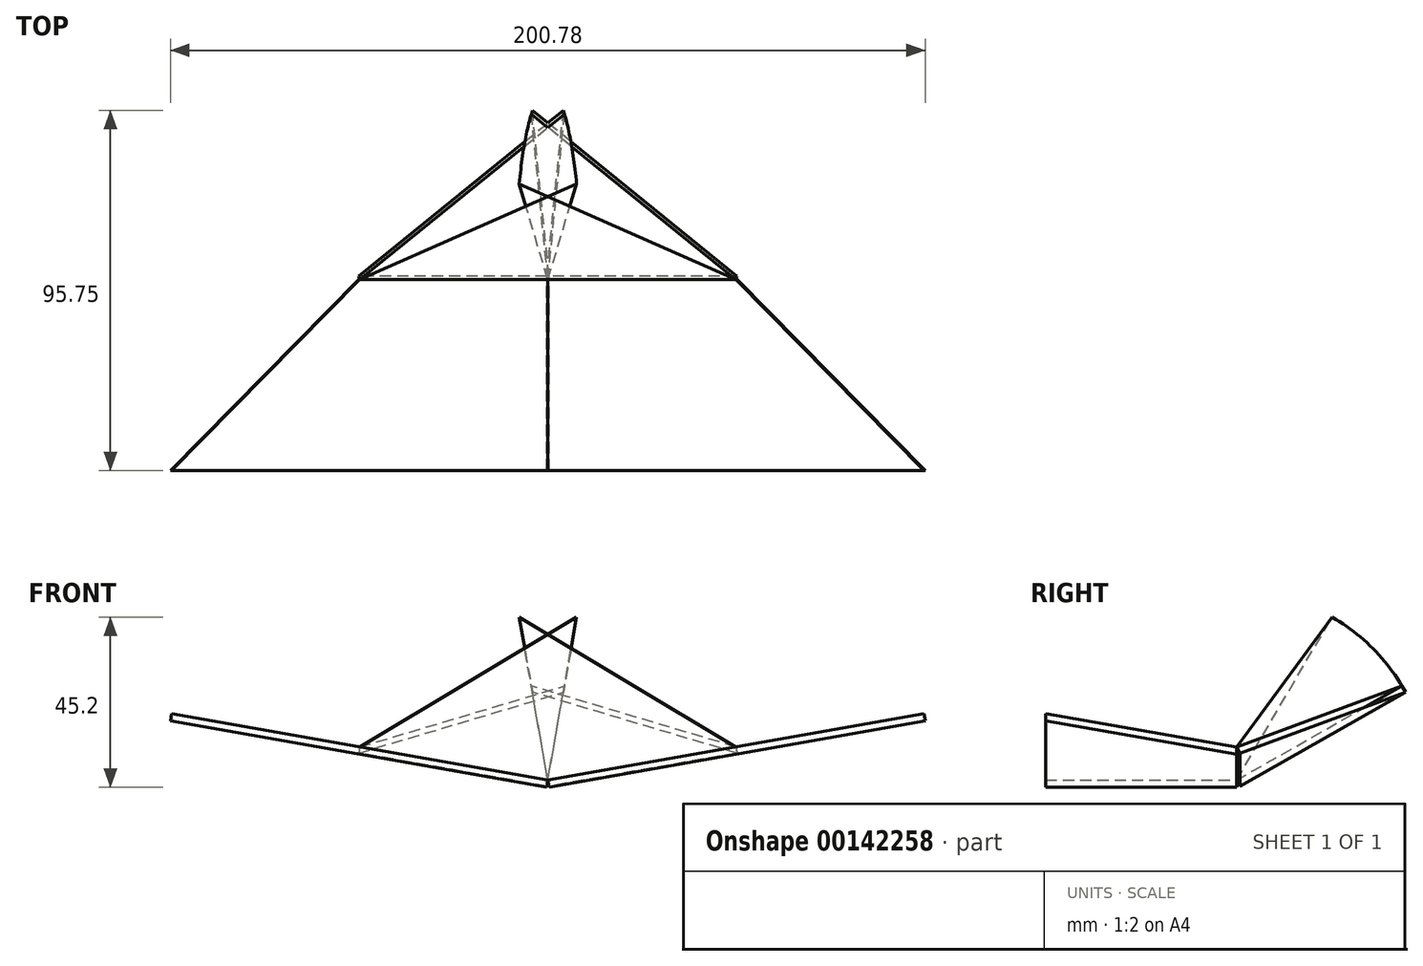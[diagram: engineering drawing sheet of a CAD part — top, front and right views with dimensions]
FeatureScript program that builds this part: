
annotation { "Feature Type Name" : "Feature", "Feature Type Description" : "" }
export const myFeature = defineFeature(function(context is Context, id is Id, definition is map)
    precondition{}
    {
        {
            var Q0;
            Q0=qCreatedBy(makeId("Top.planeOp"),FACE);
            var sketch = newSketch(context, id + "F0", { "sketchPlane" : qUnion([Q0])});
            skLineSegment(sketch, "E0", {"start": v(-101.6, 0) * mm, "end": v(0, 0) * mm});
            skLineSegment(sketch, "E1", {"start": v(-101.6, 0) * mm, "end": v(-50.8, 50.8) * mm});
            skLineSegment(sketch, "E2", {"start": v(101.6, 0) * mm, "end": v(50.8, 50.8) * mm});
            skPoint(sketch, "E3", {"position": v(0, 0) * mm});
            skLineSegment(sketch, "E4", {"start": v(0, 0) * mm, "end": v(0, 50.8) * mm});
            skLineSegment(sketch, "E5", {"start": v(50.8, 50.8) * mm, "end": v(0, 50.8) * mm});
            skLineSegment(sketch, "E6", {"start": v(0, 0) * mm, "end": v(101.6, 0) * mm});
            skLineSegment(sketch, "E7", {"start": v(0, 50.8) * mm, "end": v(-50.8, 50.8) * mm});
            skLineSegment(sketch, "E8", {"start": v(0, 50.8) * mm, "end": v(0, 101.6) * mm});
            skLineSegment(sketch, "E9", {"start": v(-50.8, 50.8) * mm, "end": v(0, 101.6) * mm});
            skLineSegment(sketch, "E10", {"start": v(50.8, 50.8) * mm, "end": v(0, 101.6) * mm});
            skSolve(sketch);
        }
        {
            var Q0;
            Q0=makeQuery(id+"F0.imprint","IMPRINT",FACE,{"disambiguationData":[TD([[makeQuery(id+"F0.imprint","IMPRINT",EDGE,{"derivedFrom":sQuery(id+"F0.wireOp",EDGE,"E0")}),1.0]])]});
            extrude(context, id + "F1", {"entities" : qUnion([Q0]), "depth" : 1.9 * mm});
        }
        {
            var Q0;
            Q0=makeQuery(id+"F1.opExtrude","SWEPT_BODY",BODY,{"disambiguationData":[OSD([sQuery(id+"F0.wireOp",EDGE,"E0"),sQuery(id+"F0.wireOp",EDGE,"E1"),sQuery(id+"F0.wireOp",EDGE,"E4"),sQuery(id+"F0.wireOp",EDGE,"E7")])]});
            var Q1;
            Q1=makeQuery(id+"F1.opExtrude","CAP_EDGE",EDGE,{"disambiguationData":[OSD([sQuery(id+"F0.wireOp",EDGE,"E4")])],"isStart":false});
            transform(context, id + "F2", {"entities" : qUnion([Q0]), "transformType" : TransformType.ROTATION, "transformAxis" : qUnion([Q1]), "angle" : 10 * degree, "makeCopy" : false});
        }
        {
            var Q0;
            Q0=makeQuery(id+"F0.imprint","IMPRINT",FACE,{"disambiguationData":[TD([[makeQuery(id+"F0.imprint","IMPRINT",EDGE,{"derivedFrom":sQuery(id+"F0.wireOp",EDGE,"E2")}),1.0]])]});
            extrude(context, id + "F3", {"entities" : qUnion([Q0]), "depth" : 1.9 * mm});
        }
        {
            var Q0;
            Q0=makeQuery(id+"F3.opExtrude","SWEPT_BODY",BODY,{"disambiguationData":[OSD([sQuery(id+"F0.wireOp",EDGE,"E2"),sQuery(id+"F0.wireOp",EDGE,"E4"),sQuery(id+"F0.wireOp",EDGE,"E5"),sQuery(id+"F0.wireOp",EDGE,"E6")])]});
            var Q1;
            Q1=makeQuery(id+"F1.opExtrude","CAP_EDGE",EDGE,{"disambiguationData":[OSD([sQuery(id+"F0.wireOp",EDGE,"E4")])],"isStart":false});
            transform(context, id + "F4", {"entities" : qUnion([Q0]), "transformType" : TransformType.ROTATION, "transformAxis" : qUnion([Q1]), "angle" : 10 * degree, "oppositeDirection" : true, "makeCopy" : false});
        }
        {
            var Q0;
            Q0=makeQuery(id+"F0.imprint","IMPRINT",FACE,{"disambiguationData":[TD([[makeQuery(id+"F0.imprint","IMPRINT",EDGE,{"derivedFrom":sQuery(id+"F0.wireOp",EDGE,"E7")}),-1.0]])]});
            extrude(context, id + "F5", {"entities" : qUnion([Q0]), "depth" : 1.9 * mm});
        }
        {
            var Q0;
            Q0=makeQuery(id+"F5.opExtrude","SWEPT_BODY",BODY,{"disambiguationData":[OSD([sQuery(id+"F0.wireOp",EDGE,"E7"),sQuery(id+"F0.wireOp",EDGE,"E8"),sQuery(id+"F0.wireOp",EDGE,"E9")])]});
            var Q1;
            Q1=makeQuery(id+"F5.opExtrude","CAP_EDGE",EDGE,{"disambiguationData":[OSD([sQuery(id+"F0.wireOp",EDGE,"E8")])],"isStart":false});
            transform(context, id + "F6", {"entities" : qUnion([Q0]), "transformType" : TransformType.ROTATION, "transformAxis" : qUnion([Q1]), "angle" : 10 * degree, "makeCopy" : false});
        }
        {
            var Q0;
            Q0=makeQuery(id+"F5.opExtrude","SWEPT_BODY",BODY,{"disambiguationData":[OSD([sQuery(id+"F0.wireOp",EDGE,"E7"),sQuery(id+"F0.wireOp",EDGE,"E8"),sQuery(id+"F0.wireOp",EDGE,"E9")])]});
            var Q1;
            Q1=makeQuery(id+"F1.opExtrude","CAP_EDGE",EDGE,{"disambiguationData":[OSD([sQuery(id+"F0.wireOp",EDGE,"E7")])],"isStart":false});
            transform(context, id + "F7", {"entities" : qUnion([Q0]), "transformType" : TransformType.ROTATION, "transformAxis" : qUnion([Q1]), "angle" : 30 * degree, "oppositeDirection" : true, "makeCopy" : false});
        }
        {
            var Q0;
            Q0=makeQuery(id+"F0.imprint","IMPRINT",FACE,{"disambiguationData":[TD([[makeQuery(id+"F0.imprint","IMPRINT",EDGE,{"derivedFrom":sQuery(id+"F0.wireOp",EDGE,"E5")}),-1.0]])]});
            extrude(context, id + "F8", {"entities" : qUnion([Q0]), "depth" : 1.9 * mm});
        }
        {
            var Q0;
            Q0=makeQuery(id+"F8.opExtrude","SWEPT_BODY",BODY,{"disambiguationData":[OSD([sQuery(id+"F0.wireOp",EDGE,"E5"),sQuery(id+"F0.wireOp",EDGE,"E8"),sQuery(id+"F0.wireOp",EDGE,"E10")])]});
            var Q1;
            Q1=makeQuery(id+"F8.opExtrude","CAP_EDGE",EDGE,{"disambiguationData":[OSD([sQuery(id+"F0.wireOp",EDGE,"E8")])],"isStart":false});
            transform(context, id + "F9", {"entities" : qUnion([Q0]), "transformType" : TransformType.ROTATION, "transformAxis" : qUnion([Q1]), "angle" : 10 * degree, "oppositeDirection" : true, "makeCopy" : false});
        }
        {
            var Q0;
            Q0=makeQuery(id+"F8.opExtrude","SWEPT_BODY",BODY,{"disambiguationData":[OSD([sQuery(id+"F0.wireOp",EDGE,"E5"),sQuery(id+"F0.wireOp",EDGE,"E8"),sQuery(id+"F0.wireOp",EDGE,"E10")])]});
            var Q1;
            Q1=makeQuery(id+"F3.opExtrude","CAP_EDGE",EDGE,{"disambiguationData":[OSD([sQuery(id+"F0.wireOp",EDGE,"E5")])],"isStart":false});
            transform(context, id + "F10", {"entities" : qUnion([Q0]), "transformType" : TransformType.ROTATION, "transformAxis" : qUnion([Q1]), "angle" : 30 * degree, "oppositeDirection" : true, "makeCopy" : false});
        }
        {
            var Q0;
            Q0=makeQuery(id+"F5.opExtrude","CAP_FACE",FACE,{"disambiguationData":[OSD([sQuery(id+"F0.wireOp",EDGE,"E7"),sQuery(id+"F0.wireOp",EDGE,"E8"),sQuery(id+"F0.wireOp",EDGE,"E9")])],"isStart":false});
            var Q1;
            Q1=makeQuery(id+"F1.opExtrude","CAP_EDGE",EDGE,{"disambiguationData":[OSD([sQuery(id+"F0.wireOp",EDGE,"E7")])],"isStart":false});
            revolve(context, id + "F11", {"entities" : qUnion([Q0]), "axis" : qUnion([Q1]), "revolveType" : RevolveType.ONE_DIRECTION, "oppositeDirection" : true, "angle" : 30 * degree});
        }
        {
            var Q0;
            Q0=makeQuery(id+"F8.opExtrude","CAP_FACE",FACE,{"disambiguationData":[OSD([sQuery(id+"F0.wireOp",EDGE,"E5"),sQuery(id+"F0.wireOp",EDGE,"E8"),sQuery(id+"F0.wireOp",EDGE,"E10")])],"isStart":false});
            var Q1;
            Q1=makeQuery(id+"F3.opExtrude","CAP_EDGE",EDGE,{"disambiguationData":[OSD([sQuery(id+"F0.wireOp",EDGE,"E5")])],"isStart":false});
            revolve(context, id + "F12", {"entities" : qUnion([Q0]), "axis" : qUnion([Q1]), "revolveType" : RevolveType.ONE_DIRECTION, "oppositeDirection" : true, "angle" : 30 * degree});
        }
    });
